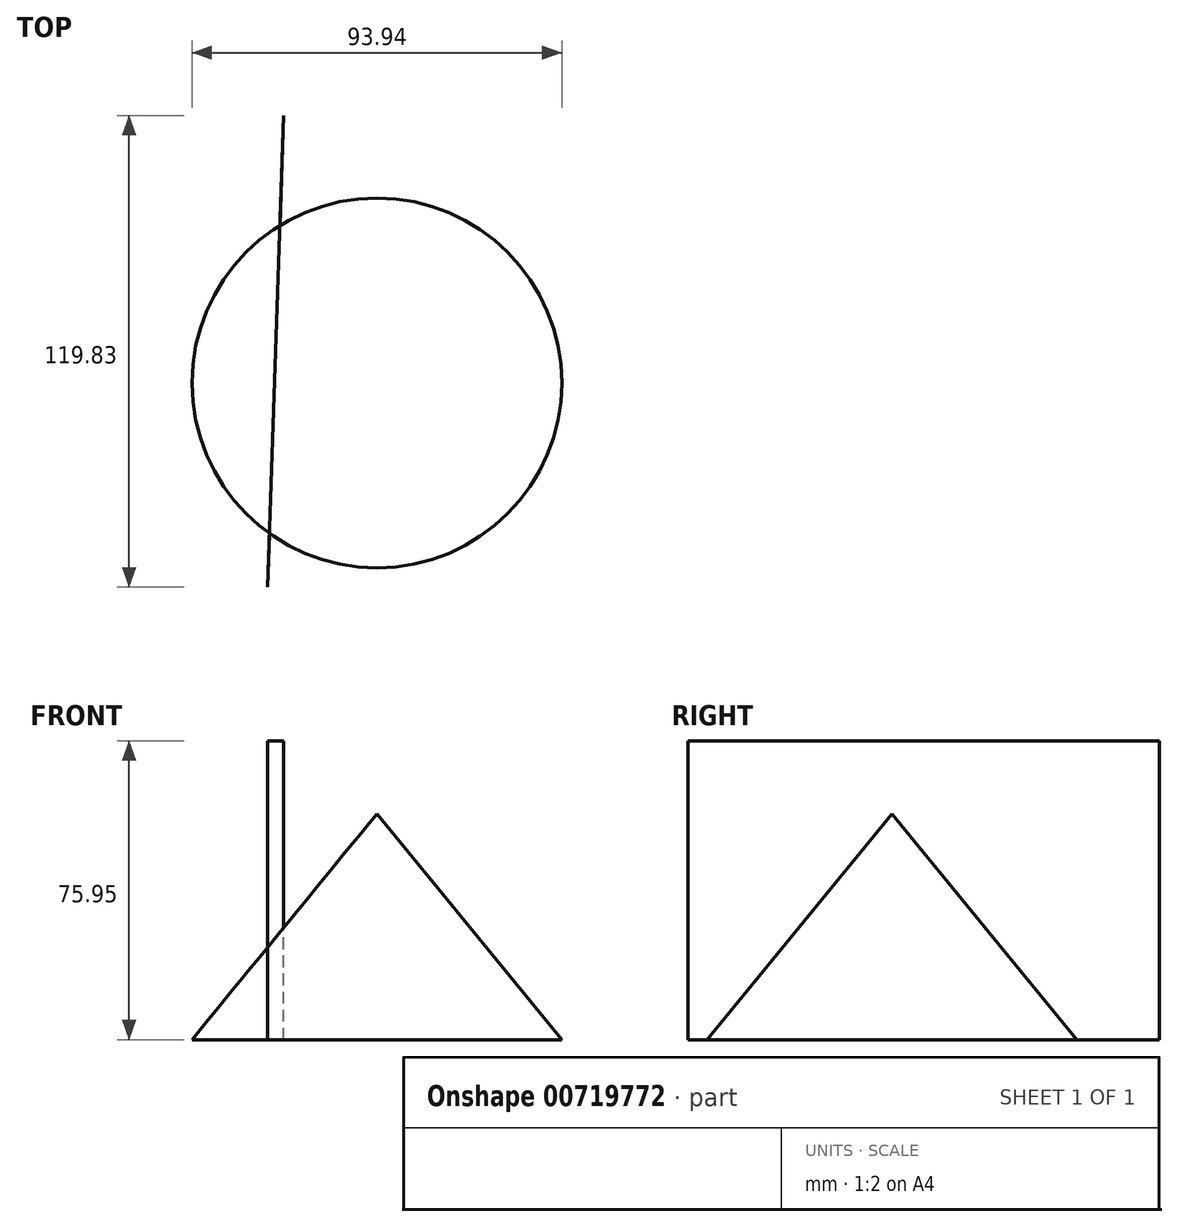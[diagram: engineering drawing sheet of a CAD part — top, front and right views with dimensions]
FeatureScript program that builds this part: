
annotation { "Feature Type Name" : "Feature", "Feature Type Description" : "" }
export const myFeature = defineFeature(function(context is Context, id is Id, definition is map)
    precondition{}
    {
        {
            var Q0;
            Q0=qCreatedBy(makeId("Right.planeOp"),FACE);
            var sketch = newSketch(context, id + "F0", { "sketchPlane" : qUnion([Q0])});
            skLineSegment(sketch, "E0", {"start": v(-46.97, 0) * mm, "end": v(0, 0) * mm});
            skLineSegment(sketch, "E1", {"start": v(0, 0) * mm, "end": v(0, 57.4) * mm});
            skLineSegment(sketch, "E2", {"start": v(0, 57.4) * mm, "end": v(-46.97, 0) * mm});
            skSolve(sketch);
        }
        {
            var Q0;
            Q0=sQuery(id+"F0.wireOp",EDGE,"E2");
            var Q1;
            Q1=sQuery(id+"F0.wireOp",EDGE,"E0");
            var Q2;
            Q2=sQuery(id+"F0.wireOp",EDGE,"E1");
            revolve(context, id + "F1", {"bodyType" : ToolBodyType.SURFACE, "surfaceOperationType" : NewSurfaceOperationType.NEW, "surfaceEntities" : qUnion([Q0, Q1]), "axis" : qUnion([Q2]), "revolveType" : RevolveType.FULL});
        }
        {
            var Q0;
            Q0=qCreatedBy(makeId("Top.planeOp"),FACE);
            var sketch = newSketch(context, id + "F2", { "sketchPlane" : qUnion([Q0])});
            skLineSegment(sketch, "E3", {"start": v(-23.69, 67.93) * mm, "end": v(-27.75, -51.9) * mm});
            skSolve(sketch);
        }
        {
            var Q0;
            Q0=sQuery(id+"F2.wireOp",EDGE,"E3");
            extrude(context, id + "F3", {"bodyType" : ToolBodyType.SURFACE, "surfaceEntities" : qUnion([Q0]), "depth" : 75.95 * mm, "offsetDistance" : 25.4 * mm});
        }
    });
